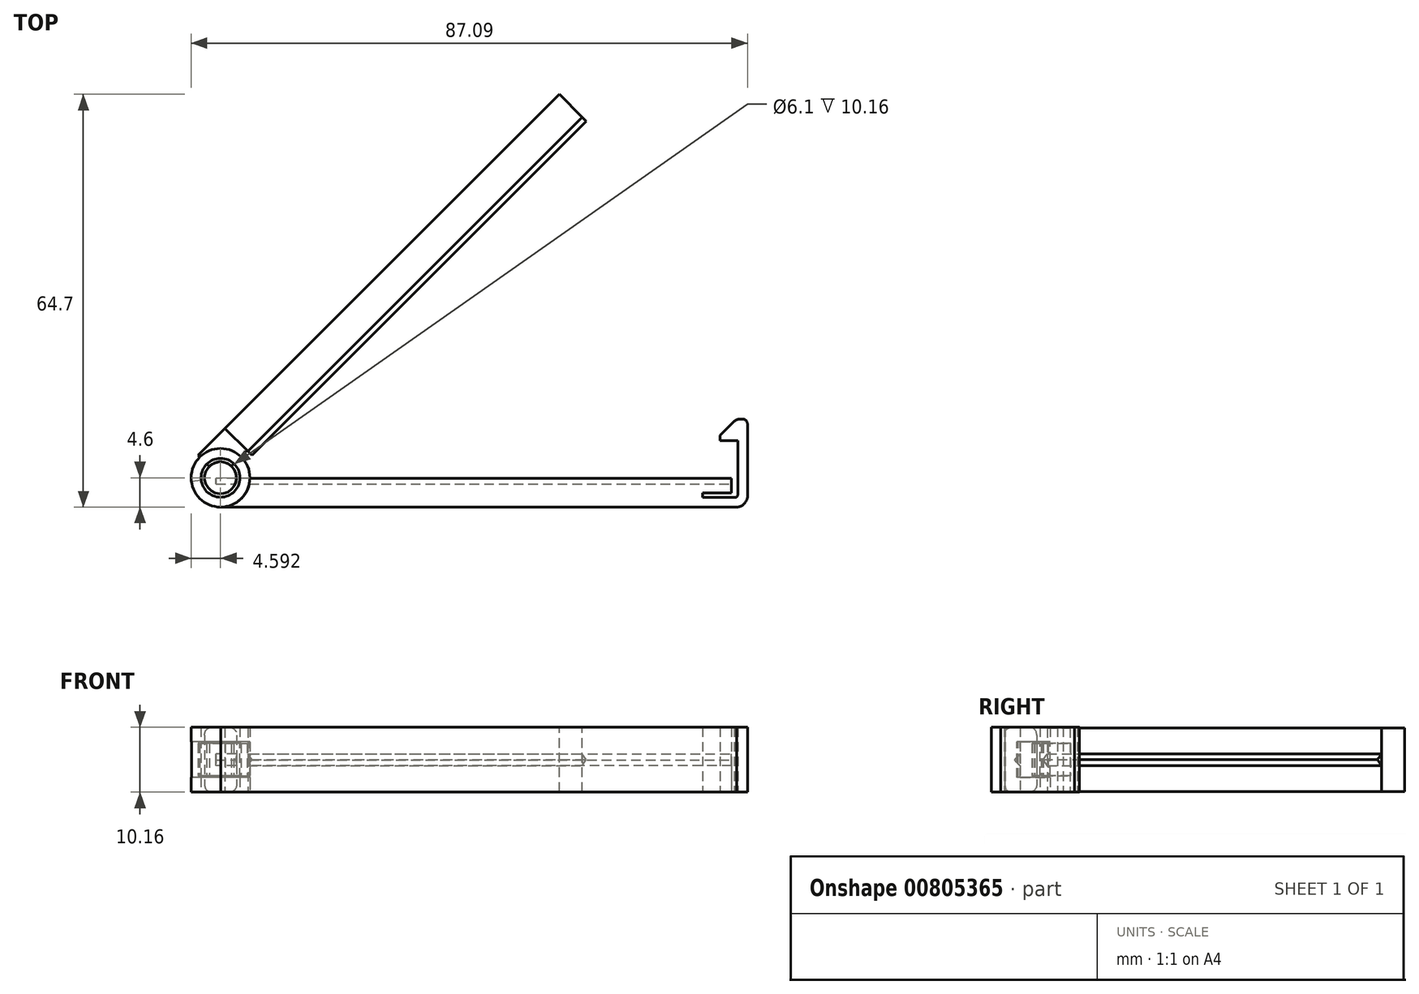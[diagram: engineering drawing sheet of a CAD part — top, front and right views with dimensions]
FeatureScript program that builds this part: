
annotation { "Feature Type Name" : "Feature", "Feature Type Description" : "" }
export const myFeature = defineFeature(function(context is Context, id is Id, definition is map)
    precondition{}
    {
        {
            var Q0;
            Q0=qCreatedBy(makeId("Top.planeOp"),FACE);
            var sketch = newSketch(context, id + "F0", { "sketchPlane" : qUnion([Q0])});
            skPoint(sketch, "E0", {"position": v(-38.94, -27.75) * mm});
            skCircle(sketch, "E1", {"center": v(-38.94, -27.75) * mm, "radius": 2.5 * mm});
            skLineSegment(sketch, "E2", {"start": v(-40.72, -25.98) * mm, "end": v(-42.48, -24.22) * mm});
            skLineSegment(sketch, "E3", {"start": v(14.08, 32.35) * mm, "end": v(17.62, 28.81) * mm});
            skLineSegment(sketch, "E4", {"start": v(-34.78, -23.44) * mm, "end": v(-33.99, -24.23) * mm});
            skLineSegment(sketch, "E5", {"start": v(-33.99, -24.23) * mm, "end": v(18.32, 28.1) * mm});
            skLineSegment(sketch, "E6", {"start": v(18.32, 28.1) * mm, "end": v(17.62, 28.81) * mm});
            skLineSegment(sketch, "E7", {"start": v(-40.72, -25.98) * mm, "end": v(-38.94, -27.75) * mm});
            skLineSegment(sketch, "E8", {"start": v(-37.25, -25.9) * mm, "end": v(-38.94, -27.75) * mm});
            skLineSegment(sketch, "E9", {"start": v(-38.24, -19.97) * mm, "end": v(-34.78, -23.44) * mm});
            skPoint(sketch, "E10", {"position": v(-38.24, -19.97) * mm});
            skLineSegment(sketch, "E11", {"start": v(-42.48, -24.22) * mm, "end": v(-38.24, -19.97) * mm});
            skLineSegment(sketch, "E12", {"start": v(-38.24, -19.97) * mm, "end": v(14.08, 32.35) * mm});
            skLineSegment(sketch, "E13", {"start": v(-37.25, -25.9) * mm, "end": v(-34.78, -23.44) * mm});
            skLineSegment(sketch, "E14", {"start": v(-34.78, -23.44) * mm, "end": v(17.62, 28.81) * mm});
            skSolve(sketch);
        }
        {
            var Q0;
            {var subQ0=sQuery(id+"F0.wireOp",EDGE,"E7");Q0=makeQuery(id+"F0.imprint","IMPRINT",FACE,{"disambiguationData":[TD([[makeQuery(id+"F0.imprint","IMPRINT",EDGE,{"derivedFrom":subQ0}),-1.0]])]});}
            var Q1;
            {var subQ0=sQuery(id+"F0.wireOp",EDGE,"E7");Q1=makeQuery(id+"F0.imprint","IMPRINT",FACE,{"disambiguationData":[TD([[makeQuery(id+"F0.imprint","IMPRINT",EDGE,{"derivedFrom":subQ0}),1.0]])]});}
            var Q2;
            Q2=sQuery(id+"F0.wireOp",EDGE,"E1");
            extrude(context, id + "F1", {"entities" : qUnion([Q0, Q1]), "surfaceEntities" : qUnion([Q2]), "endBound" : BoundingType.SYMMETRIC, "depth" : 10.16 * mm, "offsetDistance" : 25.4 * mm, "hasSecondDirection" : true, "secondDirectionOppositeDirection" : true, "secondDirectionDepth" : 5.08 * mm});
        }
        {
            var Q0;
            {var subQ0=sQuery(id+"F0.wireOp",EDGE,"E2");Q0=makeQuery(id+"F0.imprint","IMPRINT",FACE,{"disambiguationData":[TD([[makeQuery(id+"F0.imprint","IMPRINT",EDGE,{"derivedFrom":subQ0}),-1.0]])]});}
            var Q1;
            Q1=sQuery(id+"F0.wireOp",EDGE,"E2");
            var Q2;
            Q2=sQuery(id+"F0.wireOp",EDGE,"E7");
            var Q3;
            Q3=sQuery(id+"F0.wireOp",EDGE,"E8");
            var Q4;
            Q4=sQuery(id+"F0.wireOp",EDGE,"E13");
            var Q5;
            Q5=sQuery(id+"F0.wireOp",EDGE,"E9");
            var Q6;
            Q6=sQuery(id+"F0.wireOp",EDGE,"E11");
            extrude(context, id + "F2", {"entities" : qUnion([Q0]), "surfaceEntities" : qUnion([Q1, Q2, Q3, Q4, Q5, Q6]), "depth" : 2.54 * mm, "offsetDistance" : 25.4 * mm, "hasSecondDirection" : true, "secondDirectionOppositeDirection" : true, "secondDirectionDepth" : 2.54 * mm});
        }
        {
            var Q0;
            Q0=makeQuery(id+"F2.opExtrude","SWEPT_FACE",FACE,{"disambiguationData":[OSD([sQuery(id+"F0.wireOp",EDGE,"E11")])]});
            cPlane(context, id + "F3", {"entities" : qUnion([Q0]), "cplaneType" : CPlaneType.OFFSET, "offset" : 0 * mm, "width" : 152.4 * mm, "height" : 152.4 * mm});
        }
        {
            var Q0;
            Q0=qCreatedBy(id+"F3.planeOp",FACE);
            var sketch = newSketch(context, id + "F4", { "sketchPlane" : qUnion([Q0])});
            skLineSegment(sketch, "E15", {"start": v(-32.83, 2.46) * mm, "end": v(-32.83, 4.98) * mm});
            skLineSegment(sketch, "E16", {"start": v(-32.83, 4.98) * mm, "end": v(41.22, 4.98) * mm});
            skLineSegment(sketch, "E17", {"start": v(41.22, 4.98) * mm, "end": v(41.22, -5.01) * mm});
            skLineSegment(sketch, "E18", {"start": v(-32.83, -5.01) * mm, "end": v(-32.83, -2.49) * mm});
            skLineSegment(sketch, "E19", {"start": v(-32.83, -2.49) * mm, "end": v(-32.83, 2.46) * mm});
            skLineSegment(sketch, "E20", {"start": v(41.22, -5.01) * mm, "end": v(-32.83, -5.01) * mm});
            skSolve(sketch);
        }
        {
            var Q0;
            Q0=makeQuery(id+"F4.imprint","IMPRINT",FACE,{"disambiguationData":[TD([[makeQuery(id+"F4.imprint","IMPRINT",EDGE,{"derivedFrom":sQuery(id+"F4.wireOp",EDGE,"E15")}),-1.0]])]});
            var Q1;
            Q1=sQuery(id+"F4.wireOp",EDGE,"eYhi1MpS-VNJ7-cJgw-dw6u-FeKjFtGwhdby");
            var Q2;
            Q2=sQuery(id+"F4.wireOp",EDGE,"9ZvoHkQc-CYR2-l6kY-dSE9-MnJMkJ3q8TrI");
            var Q3;
            Q3=sQuery(id+"F4.wireOp",EDGE,"f5ExaPfC-bsAL-oc1X-y0ir-NheHorUjfFg7");
            var Q4;
            Q4=sQuery(id+"F4.wireOp",EDGE,"FQlkaopt-CBbH-tw7l-wL5q-EB0wirjKs65a");
            var Q5;
            Q5=sQuery(id+"F4.wireOp",EDGE,"TvMCOCRa-EXjV-ulm1-JOX4-v2cfaanY2Bvr");
            var Q6;
            Q6=sQuery(id+"F4.wireOp",EDGE,"lmaLCBwB-aZ1K-e3RN-zV7k-oPSpfsVAcoc8");
            extrude(context, id + "F5", {"entities" : qUnion([Q0]), "surfaceEntities" : qUnion([Q1, Q2, Q3, Q4, Q5, Q6]), "oppositeDirection" : true, "depth" : 5.08 * mm, "offsetDistance" : 25.4 * mm});
        }
        {
            var Q0;
            Q0=makeQuery(id+"F5.opExtrude","SWEPT_FACE",FACE,{"disambiguationData":[OSD([sQuery(id+"F4.wireOp",EDGE,"E15"),sQuery(id+"F4.wireOp",EDGE,"E18"),sQuery(id+"F4.wireOp",EDGE,"E19")])]});
            cPlane(context, id + "F6", {"entities" : qUnion([Q0]), "cplaneType" : CPlaneType.OFFSET, "offset" : 0 * mm, "width" : 152.4 * mm, "height" : 152.4 * mm});
        }
        {
            var Q0;
            Q0=qCreatedBy(id+"F6.planeOp",FACE);
            var sketch = newSketch(context, id + "F7", { "sketchPlane" : qUnion([Q0])});
            skLineSegment(sketch, "E21", {"start": v(7.84, -0.93) * mm, "end": v(6.94, 0) * mm});
            skLineSegment(sketch, "E22", {"start": v(6.94, 0) * mm, "end": v(7.83, 0.92) * mm});
            skLineSegment(sketch, "E23", {"start": v(7.83, 0.92) * mm, "end": v(7.84, -0.93) * mm});
            skSolve(sketch);
        }
        {
            var Q0;
            Q0=makeQuery(id+"F7.imprint","IMPRINT",FACE,{"disambiguationData":[TD([[makeQuery(id+"F7.imprint","IMPRINT",EDGE,{"derivedFrom":sQuery(id+"F7.wireOp",EDGE,"E21")}),-1.0]])]});
            extrude(context, id + "F8", {"entities" : qUnion([Q0]), "oppositeDirection" : true, "depth" : 74.04 * mm, "offsetDistance" : 25.4 * mm});
        }
        {
            var Q0;
            Q0=makeQuery(id+"F1.opExtrude","SWEPT_FACE",FACE,{"disambiguationData":[OSD([sQuery(id+"F0.wireOp",EDGE,"E1")])]});
            fillet(context, id + "F9", {"entities" : qUnion([Q0]), "radius" : 1.27 * mm, "tangentPropagation" : true, "rho" : 0.5, "crossSection" : FilletCrossSection.CONIC, "allowEdgeOverflow" : false});
        }
        {
            var Q0;
            Q0=qCreatedBy(makeId("Top.planeOp"),FACE);
            var sketch = newSketch(context, id + "F10", { "sketchPlane" : qUnion([Q0])});
            skLineSegment(sketch, "E24", {"start": v(-34.35, -27.85) * mm, "end": v(41.05, -27.85) * mm});
            skLineSegment(sketch, "E25", {"start": v(41.05, -27.85) * mm, "end": v(41.05, -30.15) * mm});
            skLineSegment(sketch, "E26", {"start": v(41.05, -30.15) * mm, "end": v(36.53, -30.15) * mm});
            skLineSegment(sketch, "E27", {"start": v(36.53, -30.15) * mm, "end": v(36.53, -30.85) * mm});
            skLineSegment(sketch, "E28", {"start": v(36.53, -30.85) * mm, "end": v(41.54, -30.85) * mm});
            skLineSegment(sketch, "E29", {"start": v(42.04, -30.34) * mm, "end": v(42.04, -21.96) * mm});
            skLineSegment(sketch, "E30", {"start": v(42.04, -21.96) * mm, "end": v(39.27, -21.96) * mm});
            skLineSegment(sketch, "E31", {"start": v(39.27, -21.96) * mm, "end": v(39.27, -21.1) * mm});
            skLineSegment(sketch, "E32", {"start": v(39.27, -21.1) * mm, "end": v(41.51, -18.9) * mm});
            skLineSegment(sketch, "E33", {"start": v(43.55, -19.35) * mm, "end": v(43.55, -30.85) * mm});
            skLineSegment(sketch, "E34", {"start": v(41.83, -32.35) * mm, "end": v(-38.91, -32.34) * mm});
            skFitSpline(sketch, "E35", {"points": [v(42.04, -30.34) * mm, v(41.96, -30.64) * mm, v(41.76, -30.81) * mm, v(41.54, -30.85) * mm], "startDerivative": vector(-0.13, -0.89) * mm, "endDerivative": vector(-0.72, -0.04) * mm});
            skPoint(sketch, "E36", {"position": v(-38.95, -27.75) * mm});
            skCircle(sketch, "E37", {"center": v(-38.95, -27.75) * mm, "radius": 4.6 * mm});
            skCircle(sketch, "E38", {"center": v(-38.95, -27.75) * mm, "radius": 3.05 * mm});
            skArc(sketch, "E39", {"start": v(-38.91, -32.34) * mm, "mid": v(-35.71, -31.03) * mm, "end": v(-34.35, -27.85) * mm});
            skFitSpline(sketch, "E40", {"points": [v(43.55, -30.85) * mm, v(43.45, -31.19) * mm, v(43.33, -31.44) * mm, v(43.1, -31.76) * mm, v(42.8, -32.03) * mm, v(42.4, -32.24) * mm, v(42.09, -32.32) * mm, v(41.83, -32.35) * mm], "startDerivative": vector(-0.54, -2.5) * mm, "endDerivative": vector(-2.03, -0.25) * mm});
            skFitSpline(sketch, "E41", {"points": [v(41.51, -18.9) * mm, v(41.69, -18.75) * mm, v(41.95, -18.62) * mm, v(42.21, -18.56) * mm, v(42.5, -18.55) * mm, v(42.89, -18.56) * mm, v(43.11, -18.63) * mm, v(43.3, -18.76) * mm, v(43.4, -18.87) * mm, v(43.5, -19.05) * mm, v(43.54, -19.2) * mm, v(43.55, -19.35) * mm], "startDerivative": vector(1.84, 1.62) * mm, "endDerivative": vector(0.1, -3.66) * mm});
            skLineSegment(sketch, "E42", {"start": v(41.05, -30.85) * mm, "end": v(41.05, -32.35) * mm});
            skCircle(sketch, "E43", {"center": v(-38.91, -27.78) * mm, "radius": 79.98 * mm, "construction": true});
            skLineSegment(sketch, "E44", {"start": v(-34.35, -27.85) * mm, "end": v(-35.9, -27.83) * mm});
            skLineSegment(sketch, "E45", {"start": v(-41.97, -28.16) * mm, "end": v(-43.5, -28.35) * mm});
            skSolve(sketch);
        }
        {
            var Q0;
            Q0=makeQuery(id+"F10.imprint","IMPRINT",FACE,{"disambiguationData":[TD([[makeQuery(id+"F10.imprint","IMPRINT",EDGE,{"derivedFrom":sQuery(id+"F10.wireOp",EDGE,"E24")}),-1.0]])]});
            var Q1;
            Q1=sQuery(id+"F10.wireOp",EDGE,"E39");
            var Q2;
            Q2=sQuery(id+"F10.wireOp",EDGE,"E24");
            var Q3;
            Q3=sQuery(id+"F10.wireOp",EDGE,"E25");
            var Q4;
            Q4=sQuery(id+"F10.wireOp",EDGE,"E26");
            var Q5;
            Q5=sQuery(id+"F10.wireOp",EDGE,"E27");
            var Q6;
            Q6=sQuery(id+"F10.wireOp",EDGE,"E28");
            var Q7;
            Q7=sQuery(id+"F10.wireOp",EDGE,"E35");
            var Q8;
            Q8=sQuery(id+"F10.wireOp",EDGE,"E29");
            var Q9;
            Q9=sQuery(id+"F10.wireOp",EDGE,"E30");
            var Q10;
            Q10=sQuery(id+"F10.wireOp",EDGE,"E31");
            var Q11;
            Q11=sQuery(id+"F10.wireOp",EDGE,"E32");
            var Q12;
            Q12=sQuery(id+"F10.wireOp",EDGE,"E41");
            var Q13;
            Q13=sQuery(id+"F10.wireOp",EDGE,"E33");
            var Q14;
            Q14=sQuery(id+"F10.wireOp",EDGE,"E40");
            var Q15;
            Q15=sQuery(id+"F10.wireOp",EDGE,"E34");
            extrude(context, id + "F11", {"entities" : qUnion([Q0]), "surfaceEntities" : qUnion([Q1, Q2, Q3, Q4, Q5, Q6, Q7, Q8, Q9, Q10, Q11, Q12, Q13, Q14, Q15]), "depth" : 5.08 * mm, "offsetDistance" : 25.4 * mm, "hasSecondDirection" : true, "secondDirectionOppositeDirection" : true, "secondDirectionDepth" : 5.08 * mm});
        }
        {
            var Q0;
            Q0=makeQuery(id+"F11.opExtrude","SWEPT_FACE",FACE,{"disambiguationData":[OSD([sQuery(id+"F10.wireOp",EDGE,"E25")])]});
            var sketch = newSketch(context, id + "F12", { "sketchPlane" : qUnion([Q0])});
            skLineSegment(sketch, "E46", {"start": v(-24.24, 0) * mm, "end": v(-33.92, 0) * mm, "construction": true});
            skLineSegment(sketch, "E47", {"start": v(-27.85, -0.96) * mm, "end": v(-28.75, -0.03) * mm});
            skLineSegment(sketch, "E48", {"start": v(-28.75, -0.03) * mm, "end": v(-27.85, 0.89) * mm});
            skLineSegment(sketch, "E49", {"start": v(-27.85, 0.89) * mm, "end": v(-27.85, -0.96) * mm});
            skSolve(sketch);
        }
        {
            var Q0;
            Q0=makeQuery(id+"F12.imprint","IMPRINT",FACE,{"disambiguationData":[TD([[makeQuery(id+"F12.imprint","IMPRINT",EDGE,{"derivedFrom":sQuery(id+"F12.wireOp",EDGE,"E47")}),-1.0]])]});
            extrude(context, id + "F13", {"entities" : qUnion([Q0]), "operationType" : NewBodyOperationType.REMOVE, "oppositeDirection" : true, "depth" : 80.72 * mm, "offsetDistance" : 25.4 * mm});
        }
        {
            var Q0;
            Q0=makeQuery(id+"F10.imprint","IMPRINT",FACE,{"disambiguationData":[TD([[makeQuery(id+"F10.imprint","IMPRINT",EDGE,{"derivedFrom":sQuery(id+"F10.wireOp",EDGE,"E29")}),-1.0]])]});
            extrude(context, id + "F14", {"entities" : qUnion([Q0]), "operationType" : NewBodyOperationType.ADD, "depth" : 5.08 * mm, "offsetDistance" : 25.4 * mm, "hasSecondDirection" : true, "secondDirectionOppositeDirection" : true, "secondDirectionDepth" : 5.08 * mm});
        }
        {
            var Q0;
            Q0=makeQuery(id+"F10.imprint","IMPRINT",FACE,{"disambiguationData":[TD([[makeQuery(id+"F10.imprint","IMPRINT",EDGE,{"derivedFrom":sQuery(id+"F10.wireOp",EDGE,"E38")}),-1.0]])]});
            var Q1;
            {var subQ0=sQuery(id+"F10.wireOp",EDGE,"E44");Q1=makeQuery(id+"F10.imprint","IMPRINT",FACE,{"disambiguationData":[TD([[makeQuery(id+"F10.imprint","IMPRINT",EDGE,{"derivedFrom":subQ0}),1.0]])]});}
            extrude(context, id + "F15", {"entities" : qUnion([Q0, Q1]), "operationType" : NewBodyOperationType.ADD, "endBound" : BoundingType.SYMMETRIC, "depth" : 10.16 * mm, "offsetDistance" : 25.4 * mm});
        }
        {
            var Q0;
            Q0=makeQuery(id+"F10.imprint","IMPRINT",FACE,{"disambiguationData":[TD([[makeQuery(id+"F10.imprint","IMPRINT",EDGE,{"derivedFrom":sQuery(id+"F10.wireOp",EDGE,"E38")}),-1.0]])]});
            extrude(context, id + "F16", {"entities" : qUnion([Q0]), "operationType" : NewBodyOperationType.REMOVE, "endBound" : BoundingType.SYMMETRIC, "oppositeDirection" : true, "depth" : 5.6 * mm, "offsetDistance" : 25.4 * mm});
        }
    });
